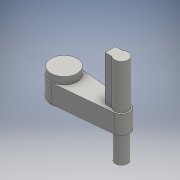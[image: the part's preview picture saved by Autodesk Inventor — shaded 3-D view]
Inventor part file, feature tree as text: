
AUTODESK INVENTOR PART (.ipt)
format: ipt  version: 2016 (Build 200138000, 138)  size: 133,632 bytes
history: native  units: mm
features: extrude x5, sketch x5
ambient origin geometry x8: Origin, YZ Plane, XZ Plane, XY Plane, X Axis, Y Axis, Z Axis, Center Point
bodies: Solid1 (feature_tree)
feature tree (10):
  extrude  "Extrusion1"  Depth=6.0mm TaperAngle=0.0deg
  extrude  "Extrusion2"  Depth=106.0mm
  extrude  "Extrusion3"  Depth=121.0mm TaperAngle=0.0deg
  extrude  "Extrusion4"  Depth=48.0mm TaperAngle=0.0deg
  extrude  "Extrusion5"  Depth=66.75mm
  sketch  "Sketch1"  dims[d0=170.0mm d1=6.0mm d2=0.0mm]
  sketch  "Sketch2"  dims[d3=178.0mm d4=106.0mm]
  sketch  "Sketch3"  dims[d5=375.0mm d6=121.0mm d7=0.0mm]
  sketch  "Sketch4"  dims[d8=170.0mm d9=48.0mm d10=0.0mm]
  sketch  "Sketch5"  dims[d11=89.0mm d12=66.75mm d13=72.5mm d14=292.0mm d15=0.0mm d16=79.0mm d17=177.92mm d18=0.0mm]
